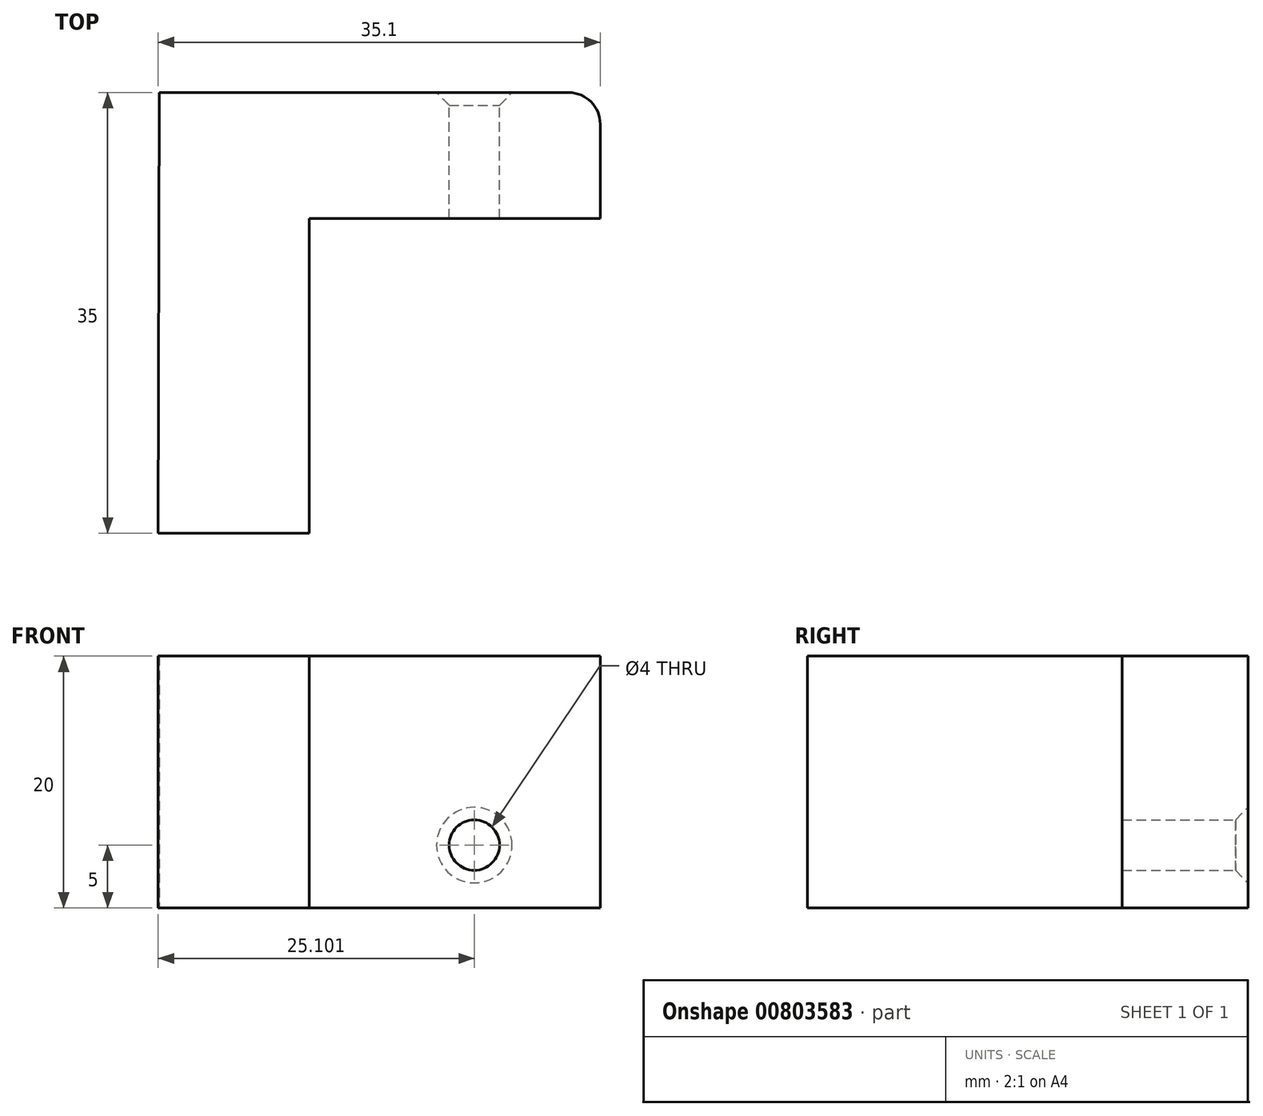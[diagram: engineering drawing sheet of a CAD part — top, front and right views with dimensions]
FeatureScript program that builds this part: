
annotation { "Feature Type Name" : "Feature", "Feature Type Description" : "" }
export const myFeature = defineFeature(function(context is Context, id is Id, definition is map)
    precondition{}
    {
        {
            var Q0;
            Q0=qCreatedBy(makeId("Top.planeOp"),FACE);
            var sketch = newSketch(context, id + "F0", { "sketchPlane" : qUnion([Q0])});
            skLineSegment(sketch, "E0", {"start": v(-4.21, -4.46) * mm, "end": v(7.79, -4.46) * mm});
            skLineSegment(sketch, "E1", {"start": v(7.79, -4.46) * mm, "end": v(7.79, 20.54) * mm});
            skLineSegment(sketch, "E2", {"start": v(7.79, 20.54) * mm, "end": v(30.9, 20.54) * mm});
            skLineSegment(sketch, "E3", {"start": v(30.9, 20.54) * mm, "end": v(30.9, 30.54) * mm});
            skLineSegment(sketch, "E4", {"start": v(30.9, 30.54) * mm, "end": v(-4.1, 30.54) * mm});
            skLineSegment(sketch, "E5", {"start": v(-4.1, 30.54) * mm, "end": v(-4.21, -4.46) * mm});
            skSolve(sketch);
        }
        {
            var Q0;
            Q0 = qSketchRegion(id + "F0", true);
            extrude(context, id + "F1", {"entities" : qUnion([Q0]), "depth" : 20 * mm, "offsetDistance" : 25 * mm});
        }
        {
            var Q0;
            Q0=makeQuery(id+"F1.opExtrude","SWEPT_FACE",FACE,{"disambiguationData":[OSD([sQuery(id+"F0.wireOp",EDGE,"E4")])]});
            var sketch = newSketch(context, id + "F2", { "sketchPlane" : qUnion([Q0])});
            skPoint(sketch, "E6", {"position": v(-20.9, 5) * mm});
            skSolve(sketch);
        }
        {
            var Q0;
            Q0=sQuery(id+"F2.wireOp",VERTEX,"E6");
            var Q1;
            Q1=makeQuery(id+"F1.opExtrude","SWEPT_BODY",BODY,{"disambiguationData":[OSD([sQuery(id+"F0.wireOp",EDGE,"E0"),sQuery(id+"F0.wireOp",EDGE,"E1"),sQuery(id+"F0.wireOp",EDGE,"E2"),sQuery(id+"F0.wireOp",EDGE,"E3"),sQuery(id+"F0.wireOp",EDGE,"E4"),sQuery(id+"F0.wireOp",EDGE,"E5")])]});
            hole(context, id + "F3", {"style" : HoleStyle.C_SINK, "endStyle" : HoleEndStyle.THROUGH, "holeDiameter" : 4 * mm, "cSinkDiameter" : 6 * mm, "cSinkAngle" : 90 * degree, "majorDiameter" : 5 * mm, "isTappedThrough" : true, "tappedDepth" : 12 * mm, "tapClearance" : 3, "locations" : qUnion([Q0]), "scope" : qUnion([Q1])});
        }
        {
            var Q0;
            Q0=makeQuery(id+"F1.opExtrude","SWEPT_EDGE",EDGE,{"disambiguationData":[OSD([sQuery(id+"F0.wireOp",EDGE,"E3"),sQuery(id+"F0.wireOp",EDGE,"E4")])]});
            fillet(context, id + "F4", {"entities" : qUnion([Q0]), "radius" : 2.5 * mm, "tangentPropagation" : true, "allowEdgeOverflow" : false});
        }
    });
